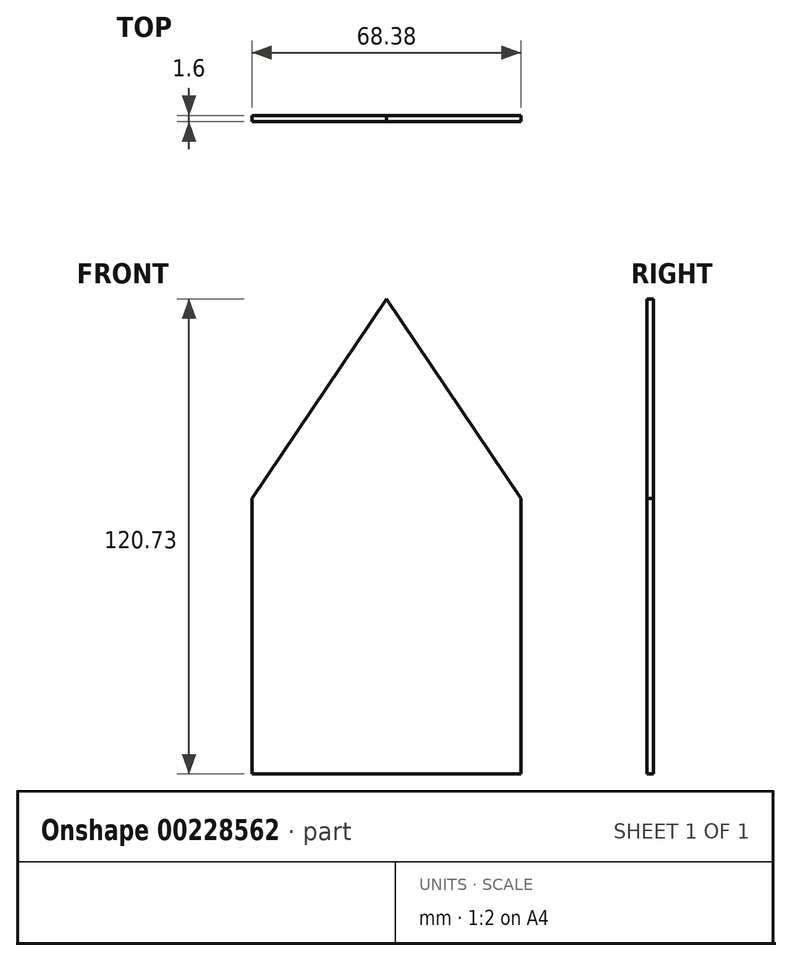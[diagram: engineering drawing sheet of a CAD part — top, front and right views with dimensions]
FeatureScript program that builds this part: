
annotation { "Feature Type Name" : "Feature", "Feature Type Description" : "" }
export const myFeature = defineFeature(function(context is Context, id is Id, definition is map)
    precondition{}
    {
        {
            var Q0;
            Q0=qCreatedBy(makeId("Front.planeOp"),FACE);
            var sketch = newSketch(context, id + "F0", { "sketchPlane" : qUnion([Q0])});
            skLineSegment(sketch, "E0", {"start": v(0, 0) * mm, "end": v(68.38, 0) * mm});
            skLineSegment(sketch, "E1", {"start": v(68.38, 0) * mm, "end": v(68.38, 69.99) * mm});
            skLineSegment(sketch, "E2", {"start": v(68.38, 69.99) * mm, "end": v(34.19, 120.73) * mm});
            skLineSegment(sketch, "E3", {"start": v(34.19, 120.73) * mm, "end": v(0, 69.99) * mm});
            skLineSegment(sketch, "E4", {"start": v(0, 69.99) * mm, "end": v(0, 0) * mm});
            skSolve(sketch);
        }
        {
            var Q0;
            Q0=makeQuery(id+"F0.imprint","IMPRINT",FACE,{"disambiguationData":[TD([[makeQuery(id+"F0.imprint","IMPRINT",EDGE,{"derivedFrom":sQuery(id+"F0.wireOp",EDGE,"E0")}),1.0]])]});
            extrude(context, id + "F1", {"entities" : qUnion([Q0]), "depth" : 1.6 * mm});
        }
    });
